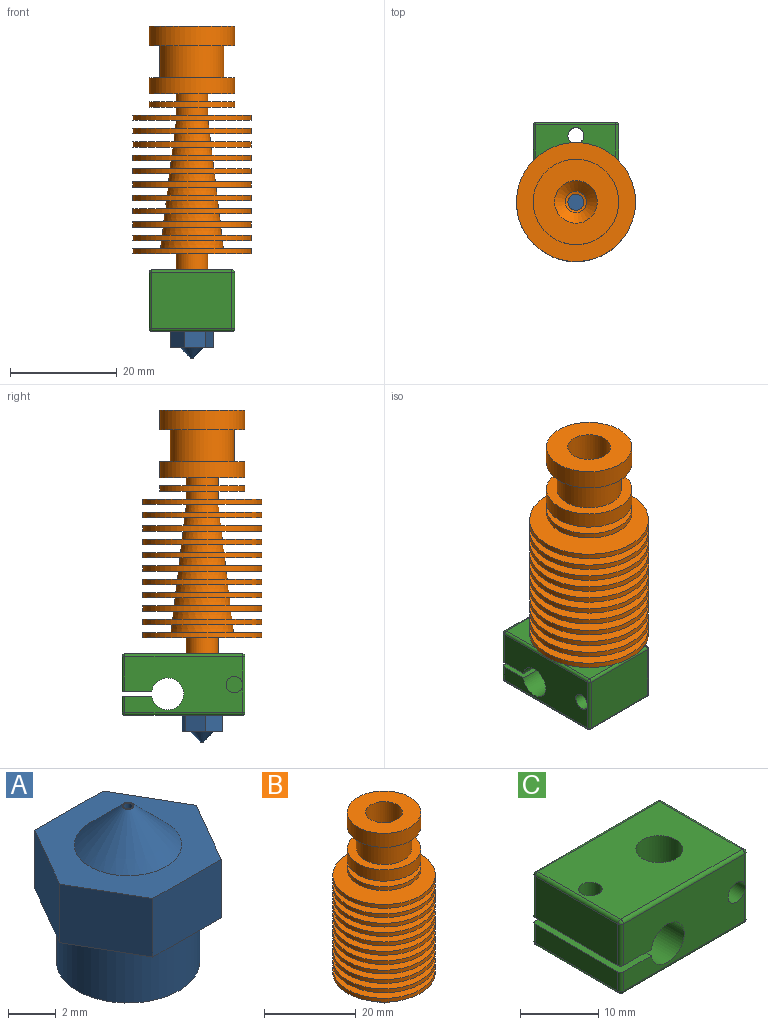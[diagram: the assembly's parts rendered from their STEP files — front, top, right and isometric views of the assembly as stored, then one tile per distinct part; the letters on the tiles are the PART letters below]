
ASSEMBLY  parts=3 mates=4
PART A: 14 faces, bbox 8.1x7x8 mm
  f0: plane 3.5x3mm, normal (0.87,-0.5,0), area 12.1mm2, adj f1,f5,f7,f8
  f1: plane 3.5x3mm, normal (0.87,0.5,0), area 12.1mm2, adj f0,f2,f7,f8
  f2: plane 4.04x3mm, normal (0,1,0), area 12.1mm2, adj f1,f3,f7,f8
  f3: plane 3.5x3mm, normal (-0.87,0.5,0), area 12.1mm2, adj f2,f4,f7,f8
  f4: plane 3.5x3mm, normal (-0.87,-0.5,0), area 12.1mm2, adj f3,f5,f7,f8
  f5: plane 4.04x3mm, normal (0,-1,0), area 12.1mm2, adj f0,f4,f7,f8
  f6: cylinder r=0.2mm len=5mm, axis (0,0,-1), area 6.3mm2, adj f9,f13
  f7: plane 8.08x7mm, normal (0,0,1), area 26.5mm2, adj f0,f1,f2,f3,f4,f5,f10
  f8: plane 8.08x7mm, normal (0,0,-1), area 14.2mm2, adj f0,f1,f2,f3,f4,f5,f12
  f9: plane 0.5x0.5mm, normal (0,0,1), area 0.1mm2, adj f6,f10
  f10: cone r=0.25mm half-angle=45deg, axis (0,0,-1), area 22.2mm2, adj f7,f9
  f11: plane 6x6mm, normal (0,0,-1), area 28.3mm2, adj f12
  f12: cylinder r=3mm len=6mm, axis (0,0,1), area 56.5mm2, adj f8,f11
  f13: plane 0.4x0.4mm, normal (0,0,1), area 0.1mm2, adj f6
PART B: 64 faces, bbox 22.3x22.3x48.7 mm
  f0: plane 22.3x22.3mm, normal (0,0,1), area 282mm2, adj f1,f63
  f1: cone r=5.7mm half-angle=6.8deg, axis (0,0,-1), area 55mm2, adj f0,f2
  f2: plane 22.3x22.3mm, normal (0,0,-1), area 288.5mm2, adj f1,f3
  f3: cylinder r=11.15mm len=22.3mm, axis (0,0,1), area 70.1mm2, adj f2,f4
  f4: plane 22.3x22.3mm, normal (0,0,1), area 292.8mm2, adj f3,f5
  f5: cone r=5.4mm half-angle=6.8deg, axis (0,0,-1), area 52.1mm2, adj f4,f6
  f6: plane 22.3x22.3mm, normal (0,0,-1), area 299mm2, adj f5,f7
  f7: cylinder r=11.15mm len=22.3mm, axis (0,0,1), area 70.1mm2, adj f6,f8
  f8: plane 22.3x22.3mm, normal (0,0,1), area 303mm2, adj f7,f9
  f9: cone r=5.1mm half-angle=6.8deg, axis (0,0,-1), area 49.3mm2, adj f8,f10
  f10: plane 22.3x22.3mm, normal (0,0,-1), area 308.9mm2, adj f9,f11
  f11: cylinder r=11.15mm len=22.3mm, axis (0,0,1), area 70.1mm2, adj f10,f12
  f12: plane 22.3x22.3mm, normal (0,0,1), area 312.7mm2, adj f11,f13
  f13: cone r=4.8mm half-angle=6.8deg, axis (0,0,-1), area 46.4mm2, adj f12,f14
  f14: plane 22.3x22.3mm, normal (0,0,-1), area 318.2mm2, adj f13,f15
  f15: cylinder r=11.15mm len=22.3mm, axis (0,0,1), area 70.1mm2, adj f14,f16
  f16: plane 22.3x22.3mm, normal (0,0,1), area 321.8mm2, adj f15,f17
  f17: cone r=4.5mm half-angle=6.8deg, axis (0,0,-1), area 43.6mm2, adj f16,f18
  f18: plane 22.3x22.3mm, normal (0,0,-1), area 327mm2, adj f17,f19
  f19: cylinder r=11.15mm len=22.3mm, axis (0,0,1), area 70.1mm2, adj f18,f20
  f20: plane 22.3x22.3mm, normal (0,0,1), area 330.3mm2, adj f19,f21
  f21: cone r=4.2mm half-angle=6.8deg, axis (0,0,-1), area 40.7mm2, adj f20,f22
  f22: plane 22.3x22.3mm, normal (0,0,-1), area 335.2mm2, adj f21,f23
  f23: cylinder r=11.15mm len=22.3mm, axis (0,0,1), area 70.1mm2, adj f22,f24
  f24: plane 22.3x22.3mm, normal (0,0,1), area 338.3mm2, adj f23,f25
  f25: cone r=3.9mm half-angle=6.8deg, axis (0,0,-1), area 37.9mm2, adj f24,f26
  f26: plane 22.3x22.3mm, normal (0,0,-1), area 342.8mm2, adj f25,f27
  f27: cylinder r=11.15mm len=22.3mm, axis (0,0,1), area 70.1mm2, adj f26,f28
  f28: plane 22.3x22.3mm, normal (0,0,1), area 345.7mm2, adj f27,f29
  f29: cone r=3.6mm half-angle=6.8deg, axis (0,0,-1), area 35mm2, adj f28,f30
  f30: plane 22.3x22.3mm, normal (0,0,-1), area 349.9mm2, adj f29,f31
  f31: cylinder r=11.15mm len=22.3mm, axis (0,0,1), area 70.1mm2, adj f30,f32
  f32: plane 22.3x22.3mm, normal (0,0,1), area 352.5mm2, adj f31,f33
  f33: cone r=3.3mm half-angle=6.8deg, axis (0,0,-1), area 32.2mm2, adj f32,f34
  f34: plane 22.3x22.3mm, normal (0,0,-1), area 356.4mm2, adj f33,f35
  f35: cylinder r=11.15mm len=22.3mm, axis (0,0,1), area 70.1mm2, adj f34,f36
  f36: plane 22.3x22.3mm, normal (0,0,1), area 358.8mm2, adj f35,f37
  f37: cone r=3mm half-angle=6.8deg, axis (0,0,-1), area 29.3mm2, adj f36,f38
  f38: plane 22.3x22.3mm, normal (0,0,-1), area 362.3mm2, adj f37,f39
  f39: cylinder r=11.15mm len=22.3mm, axis (0,0,1), area 70.1mm2, adj f38,f40
  f40: plane 22.3x22.3mm, normal (0,0,1), area 362.3mm2, adj f39,f41
  f41: cylinder r=3mm len=6mm, axis (0,0,1), area 28.3mm2, adj f40,f42
  f42: plane 16x16mm, normal (0,0,-1), area 172.8mm2, adj f41,f43
  f43: cylinder r=8mm len=16mm, axis (0,0,1), area 50.3mm2, adj f42,f44
  f44: plane 16x16mm, normal (0,0,1), area 172.8mm2, adj f43,f45
  f45: cylinder r=3mm len=6mm, axis (0,0,1), area 28.3mm2, adj f44,f46
  f46: plane 16x16mm, normal (0,0,-1), area 172.8mm2, adj f45,f47
  f47: cylinder r=8mm len=16mm, axis (0,0,1), area 150.8mm2, adj f46,f48
  f48: plane 16x16mm, normal (0,0,1), area 88mm2, adj f47,f49
  f49: cylinder r=6mm len=12mm, axis (0,0,1), area 226.2mm2, adj f48,f50
  f50: plane 16x16mm, normal (0,0,-1), area 88mm2, adj f49,f51
  f51: cylinder r=8mm len=16mm, axis (0,0,1), area 186mm2, adj f50,f52
  f52: plane 16x16mm, normal (0,0,1), area 150.8mm2, adj f51,f53
  f53: cylinder r=4mm len=8mm, axis (0,0,1), area 165.7mm2, adj f52,f54
  f54: cone r=4mm half-angle=46.2deg, axis (0,0,1), area 52.2mm2, adj f53,f55
  f55: cylinder r=2mm len=24.95mm, axis (0,0,1), area 313.5mm2, adj f54,f56
  f56: plane 7x7mm, normal (0,0,-1), area 25.9mm2, adj f55,f57
  f57: cylinder r=3.5mm len=8.24mm, axis (0,0,1), area 181.2mm2, adj f56,f58
  f58: cone r=1.5mm half-angle=74.1deg, axis (0,0,1), area 32.7mm2, adj f57,f59
  f59: cylinder r=1.5mm len=6.43mm, axis (0,0,1), area 60.6mm2, adj f58,f60
  f60: plane 6x6mm, normal (0,0,-1), area 21.2mm2, adj f59,f61
  f61: cylinder r=3mm len=6mm, axis (0,0,1), area 113.1mm2, adj f60,f62
  f62: plane 22.3x22.3mm, normal (0,0,-1), area 362.3mm2, adj f61,f63
  f63: cylinder r=11.15mm len=22.3mm, axis (0,0,1), area 70.1mm2, adj f0,f62
PART C: 37 faces, bbox 23x16x11.5 mm
  f0: plane 22x15mm, normal (0,0,-1), area 294.7mm2, adj f12,f14,f25,f30,f33,f36
  f1: plane 15x10.5mm, normal (1,0,0), area 157.5mm2, adj f22,f31,f32,f36
  f2: plane 22x15mm, normal (0,0,1), area 294.7mm2, adj f13,f14,f16,f21,f22,f23
  f3: plane 15x6.5mm, normal (-1,0,0), area 97.5mm2, adj f4,f15,f16,f17
  f4: plane 16x5.54mm, normal (0,0,-1), area 81.5mm2, adj f3,f5,f8,f9,f13,f15,f17
  f5: cylinder r=3mm len=16mm, axis (0,1,0), area 285.5mm2, adj f4,f6,f8,f9
  f6: plane 16x5.54mm, normal (0,0,1), area 81.5mm2, adj f5,f7,f8,f9,f12,f20,f24
  f7: plane 15x3mm, normal (-1,0,0), area 45mm2, adj f6,f20,f24,f25
  f8: plane 22x10.5mm, normal (0,-1,0), area 190.2mm2, adj f4,f5,f6,f10,f15,f20,f21,f30
  f9: plane 22x10.5mm, normal (0,1,0), area 197.7mm2, adj f4,f5,f6,f17,f23,f24,f32,f33
  f10: cylinder r=1.55mm len=10mm, axis (0,-1,0), area 97.4mm2, adj f8,f11,f31
  f11: plane 3.1x3.1mm, normal (0,-1,0), area 7.5mm2, adj f10
  f12: cylinder r=1.5mm len=3.5mm, axis (0,0,1), area 33mm2, adj f0,f6
  f13: cylinder r=1.5mm len=7mm, axis (0,0,1), area 66mm2, adj f2,f4
  f14: cylinder r=3mm len=11.5mm, axis (0,0,1), area 216.8mm2, adj f0,f2
  f15: cylinder r=0.5mm len=6.5mm, axis (0,0,1), area 5.1mm2, adj f3,f4,f8,f18
  f16: cylinder r=0.5mm len=15mm, axis (0,-1,0), area 11.8mm2, adj f2,f3,f18,f19
  f17: cylinder r=0.5mm len=6.5mm, axis (0,0,-1), area 5.1mm2, adj f3,f4,f9,f19
  f18: sphere r=0.5mm, area 0.4mm2, adj f15,f16,f21
  f19: sphere r=0.5mm, area 0.4mm2, adj f16,f17,f23
  f20: cylinder r=0.5mm len=3mm, axis (0,0,1), area 2.4mm2, adj f6,f7,f8,f26
  f21: cylinder r=0.5mm len=22mm, axis (1,0,0), area 17.3mm2, adj f2,f8,f18,f27
  f22: cylinder r=0.5mm len=15mm, axis (0,1,0), area 11.8mm2, adj f1,f2,f27,f28
  f23: cylinder r=0.5mm len=22mm, axis (-1,0,0), area 17.3mm2, adj f2,f9,f19,f28
  f24: cylinder r=0.5mm len=3mm, axis (0,0,-1), area 2.4mm2, adj f6,f7,f9,f29
  f25: cylinder r=0.5mm len=15mm, axis (0,1,0), area 11.8mm2, adj f0,f7,f26,f29
  f26: sphere r=0.5mm, area 0.4mm2, adj f20,f25,f30
  f27: sphere r=0.5mm, area 0.4mm2, adj f21,f22,f31
  f28: sphere r=0.5mm, area 0.4mm2, adj f22,f23,f32
  f29: sphere r=0.5mm, area 0.4mm2, adj f24,f25,f33
  f30: cylinder r=0.5mm len=22mm, axis (-1,0,0), area 17.3mm2, adj f0,f8,f26,f34
  f31: cylinder r=0.5mm len=10.5mm, axis (0,0,-1), area 8.2mm2, adj f1,f8,f10,f27,f34
  f32: cylinder r=0.5mm len=10.5mm, axis (0,0,1), area 8.2mm2, adj f1,f9,f28,f35
  f33: cylinder r=0.5mm len=22mm, axis (1,0,0), area 17.3mm2, adj f0,f9,f29,f35
  f34: sphere r=0.5mm, area 0.4mm2, adj f30,f31,f36
  f35: sphere r=0.5mm, area 0.4mm2, adj f32,f33,f36
  f36: cylinder r=0.5mm len=15mm, axis (0,-1,0), area 11.8mm2, adj f0,f1,f34,f35
PLACE A rot(axis=(0.43,0.9,0),180deg) t=(-6.41,22.84,-22.76)mm
PLACE B t=(-6.41,22.84,-8.26)mm fixed
PLACE C rot(axis=(0,0,-1),90deg) t=(-6.41,26.34,-17.01)mm
MATE cylindrical C.f14 <-> A.f12  axis (0,0,1) through (-6.41,22.84,-17.01)mm
MATE cylindrical C.f14 <-> B.f1  axis (0,0,1) through (-6.41,22.84,-17.01)mm
MATE planar C.f2 <-> B.f1  axis (0,0,1) through (-6.41,26.46,-11.26)mm
MATE planar A.f8 <-> C.f0  axis (0,0,1) through (-3.86,19.7,-22.76)mm
